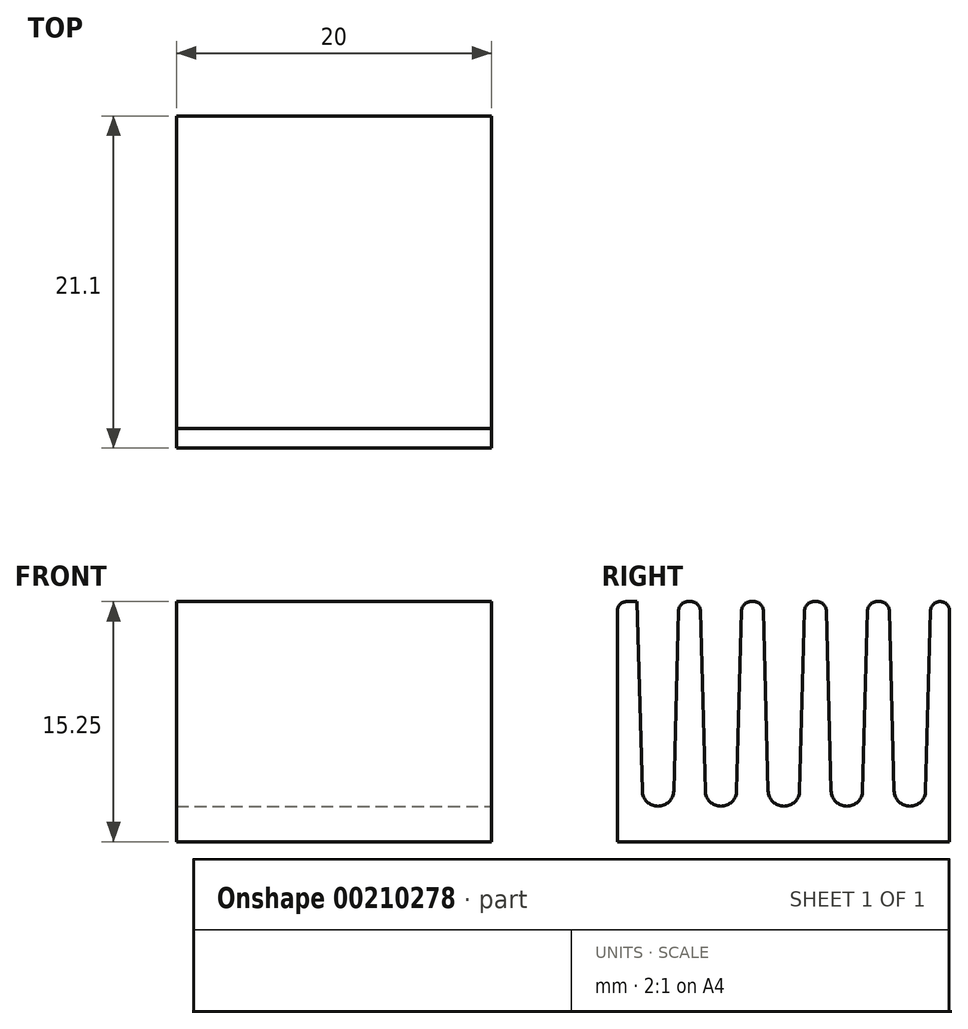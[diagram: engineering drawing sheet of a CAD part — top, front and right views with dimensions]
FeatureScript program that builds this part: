
annotation { "Feature Type Name" : "Feature", "Feature Type Description" : "" }
export const myFeature = defineFeature(function(context is Context, id is Id, definition is map)
    precondition{}
    {
        {
            var Q0;
            Q0=qCreatedBy(makeId("Top.planeOp"),FACE);
            var sketch = newSketch(context, id + "F0", { "sketchPlane" : qUnion([Q0])});
            skLineSegment(sketch, "E0.bottom", {"start": v(0, 0) * mm, "end": v(20, 0) * mm});
            skLineSegment(sketch, "E0.top", {"start": v(0, 21.1) * mm, "end": v(20, 21.1) * mm});
            skLineSegment(sketch, "E0.left", {"start": v(0, 0) * mm, "end": v(0, 21.1) * mm});
            skLineSegment(sketch, "E0.right", {"start": v(20, 0) * mm, "end": v(20, 21.1) * mm});
            skSolve(sketch);
        }
        {
            var Q0;
            Q0=qSketchRegion(id+"F0",true);
            extrude(context, id + "F1", {"entities" : qUnion([Q0]), "depth" : 15.25 * mm});
        }
        {
            var Q0;
            Q0=makeQuery(id+"F1.opExtrude","SWEPT_FACE",FACE,{"disambiguationData":[OSD([sQuery(id+"F0.wireOp",EDGE,"E0.right")])]});
            var sketch = newSketch(context, id + "F2", { "sketchPlane" : qUnion([Q0])});
            skSolve(sketch);
        }
        {
            var Q0;
            {var subQ0=sQuery(id+"F0.wireOp",EDGE,"E0.right");Q0=makeQuery(id+"F2.imprint","IMPRINT",FACE,{"disambiguationData":[TD([[makeQuery(id+"F2.imprint","IMPRINT",EDGE,{"derivedFrom":makeQuery(id+"F1.opExtrude","CAP_EDGE",EDGE,{"disambiguationData":[OSD([subQ0])],"isStart":true})}),1.0]])]});}
            var sketch = newSketch(context, id + "F3", { "sketchPlane" : qUnion([Q0])});
            skLineSegment(sketch, "E1", {"start": v(1.25, 15.25) * mm, "end": v(1.57, 3.22) * mm});
            skLineSegment(sketch, "E2", {"start": v(3.58, 3.22) * mm, "end": v(3.9, 15.25) * mm});
            skArc(sketch, "E3", {"start": v(1.57, 3.22) * mm, "mid": v(2.57, 2.25) * mm, "end": v(3.57, 3.22) * mm});
            skLineSegment(sketch, "E4.1.0.0", {"start": v(5.25, 15.25) * mm, "end": v(5.57, 3.22) * mm});
            skLineSegment(sketch, "E4.1.0.1", {"start": v(7.57, 3.22) * mm, "end": v(7.9, 15.25) * mm});
            skArc(sketch, "E4.1.0.2", {"start": v(5.57, 3.22) * mm, "mid": v(6.57, 2.25) * mm, "end": v(7.57, 3.22) * mm});
            skLineSegment(sketch, "E4.2.0.0", {"start": v(9.25, 15.25) * mm, "end": v(9.57, 3.22) * mm});
            skLineSegment(sketch, "E4.2.0.1", {"start": v(11.58, 3.22) * mm, "end": v(11.9, 15.25) * mm});
            skArc(sketch, "E4.2.0.2", {"start": v(9.57, 3.22) * mm, "mid": v(10.57, 2.25) * mm, "end": v(11.57, 3.22) * mm});
            skLineSegment(sketch, "E4.3.0.0", {"start": v(13.25, 15.25) * mm, "end": v(13.58, 3.22) * mm});
            skLineSegment(sketch, "E4.3.0.1", {"start": v(15.58, 3.22) * mm, "end": v(15.9, 15.25) * mm});
            skArc(sketch, "E4.3.0.2", {"start": v(13.57, 3.22) * mm, "mid": v(14.57, 2.25) * mm, "end": v(15.57, 3.22) * mm});
            skLineSegment(sketch, "E4.4.0.0", {"start": v(17.25, 15.25) * mm, "end": v(17.57, 3.22) * mm});
            skLineSegment(sketch, "E4.4.0.1", {"start": v(19.58, 3.22) * mm, "end": v(19.9, 15.25) * mm});
            skArc(sketch, "E4.4.0.2", {"start": v(17.57, 3.22) * mm, "mid": v(18.57, 2.25) * mm, "end": v(19.57, 3.22) * mm});
            skLineSegment(sketch, "E4.direction1", {"start": v(1.57, 3.22) * mm, "end": v(5.58, 3.22) * mm, "construction": true});
            skSolve(sketch);
        }
        {
            var Q0;
            {var subQ2=sQuery(id+"F3.wireOp",EDGE,"E1");Q0=makeQuery(id+"F3.imprint","IMPRINT",FACE,{"disambiguationData":[TD([[makeQuery(id+"F3.imprint","IMPRINT",EDGE,{"derivedFrom":subQ2}),1.0]])]});}
            var Q1;
            {var subQ2=sQuery(id+"F3.wireOp",EDGE,"E4.1.0.0");Q1=makeQuery(id+"F3.imprint","IMPRINT",FACE,{"disambiguationData":[TD([[makeQuery(id+"F3.imprint","IMPRINT",EDGE,{"derivedFrom":subQ2}),1.0]])]});}
            var Q2;
            {var subQ2=sQuery(id+"F3.wireOp",EDGE,"E4.2.0.0");Q2=makeQuery(id+"F3.imprint","IMPRINT",FACE,{"disambiguationData":[TD([[makeQuery(id+"F3.imprint","IMPRINT",EDGE,{"derivedFrom":subQ2}),1.0]])]});}
            var Q3;
            {var subQ2=sQuery(id+"F3.wireOp",EDGE,"E4.3.0.0");Q3=makeQuery(id+"F3.imprint","IMPRINT",FACE,{"disambiguationData":[TD([[makeQuery(id+"F3.imprint","IMPRINT",EDGE,{"derivedFrom":subQ2}),1.0]])]});}
            var Q4;
            {var subQ2=sQuery(id+"F3.wireOp",EDGE,"E4.4.0.0");Q4=makeQuery(id+"F3.imprint","IMPRINT",FACE,{"disambiguationData":[TD([[makeQuery(id+"F3.imprint","IMPRINT",EDGE,{"derivedFrom":subQ2}),1.0]])]});}
            extrude(context, id + "F4", {"entities" : qUnion([Q0, Q1, Q2, Q3, Q4]), "operationType" : NewBodyOperationType.REMOVE, "endBound" : BoundingType.THROUGH_ALL, "oppositeDirection" : true, "depth" : 25 * mm});
        }
        {
            var Q0;
            Q0=makeQuery(id+"F1.opExtrude","CAP_EDGE",EDGE,{"disambiguationData":[OSD([sQuery(id+"F0.wireOp",EDGE,"E0.bottom")])],"isStart":false});
            var Q1;
            Q1=makeQuery(id+"F4.boolean.opBoolean","COPY",EDGE,{"derivedFrom":makeQuery(id+"F4.opExtrude","SWEPT_EDGE",EDGE,{"disambiguationData":[OSD([sQuery(id+"F0.wireOp",EDGE,"E0.right"),sQuery(id+"F3.wireOp",EDGE,"E1")])]})});
            var Q2;
            Q2=makeQuery(id+"F4.boolean.opBoolean","COPY",EDGE,{"derivedFrom":makeQuery(id+"F4.opExtrude","SWEPT_EDGE",EDGE,{"disambiguationData":[OSD([sQuery(id+"F0.wireOp",EDGE,"E0.right"),sQuery(id+"F3.wireOp",EDGE,"E2")])]})});
            var Q3;
            Q3=makeQuery(id+"F4.boolean.opBoolean","COPY",EDGE,{"derivedFrom":makeQuery(id+"F4.opExtrude","SWEPT_EDGE",EDGE,{"disambiguationData":[OSD([sQuery(id+"F0.wireOp",EDGE,"E0.right"),sQuery(id+"F3.wireOp",EDGE,"E4.1.0.0")])]})});
            var Q4;
            Q4=makeQuery(id+"F4.boolean.opBoolean","COPY",EDGE,{"derivedFrom":makeQuery(id+"F4.opExtrude","SWEPT_EDGE",EDGE,{"disambiguationData":[OSD([sQuery(id+"F0.wireOp",EDGE,"E0.right"),sQuery(id+"F3.wireOp",EDGE,"E4.1.0.1")])]})});
            var Q5;
            Q5=makeQuery(id+"F4.boolean.opBoolean","COPY",EDGE,{"derivedFrom":makeQuery(id+"F4.opExtrude","SWEPT_EDGE",EDGE,{"disambiguationData":[OSD([sQuery(id+"F0.wireOp",EDGE,"E0.right"),sQuery(id+"F3.wireOp",EDGE,"E4.2.0.0")])]})});
            var Q6;
            Q6=makeQuery(id+"F4.boolean.opBoolean","COPY",EDGE,{"derivedFrom":makeQuery(id+"F4.opExtrude","SWEPT_EDGE",EDGE,{"disambiguationData":[OSD([sQuery(id+"F0.wireOp",EDGE,"E0.right"),sQuery(id+"F3.wireOp",EDGE,"E4.2.0.1")])]})});
            var Q7;
            Q7=makeQuery(id+"F4.boolean.opBoolean","COPY",EDGE,{"derivedFrom":makeQuery(id+"F4.opExtrude","SWEPT_EDGE",EDGE,{"disambiguationData":[OSD([sQuery(id+"F0.wireOp",EDGE,"E0.right"),sQuery(id+"F3.wireOp",EDGE,"E4.3.0.0")])]})});
            var Q8;
            Q8=makeQuery(id+"F4.boolean.opBoolean","COPY",EDGE,{"derivedFrom":makeQuery(id+"F4.opExtrude","SWEPT_EDGE",EDGE,{"disambiguationData":[OSD([sQuery(id+"F0.wireOp",EDGE,"E0.right"),sQuery(id+"F3.wireOp",EDGE,"E4.3.0.1")])]})});
            var Q9;
            Q9=makeQuery(id+"F4.boolean.opBoolean","COPY",EDGE,{"derivedFrom":makeQuery(id+"F4.opExtrude","SWEPT_EDGE",EDGE,{"disambiguationData":[OSD([sQuery(id+"F0.wireOp",EDGE,"E0.right"),sQuery(id+"F3.wireOp",EDGE,"E4.4.0.0")])]})});
            var Q10;
            Q10=makeQuery(id+"F4.boolean.opBoolean","COPY",EDGE,{"derivedFrom":makeQuery(id+"F4.opExtrude","SWEPT_EDGE",EDGE,{"disambiguationData":[OSD([sQuery(id+"F0.wireOp",EDGE,"E0.right"),sQuery(id+"F3.wireOp",EDGE,"E4.4.0.1")])]})});
            var Q11;
            Q11=makeQuery(id+"F1.opExtrude","CAP_EDGE",EDGE,{"disambiguationData":[OSD([sQuery(id+"F0.wireOp",EDGE,"E0.top")])],"isStart":false});
            fillet(context, id + "F5", {"entities" : qUnion([Q0, Q1, Q2, Q3, Q4, Q5, Q6, Q7, Q8, Q9, Q10, Q11]), "radius" : .6 * mm, "tangentPropagation" : true, "allowEdgeOverflow" : false});
        }
    });
